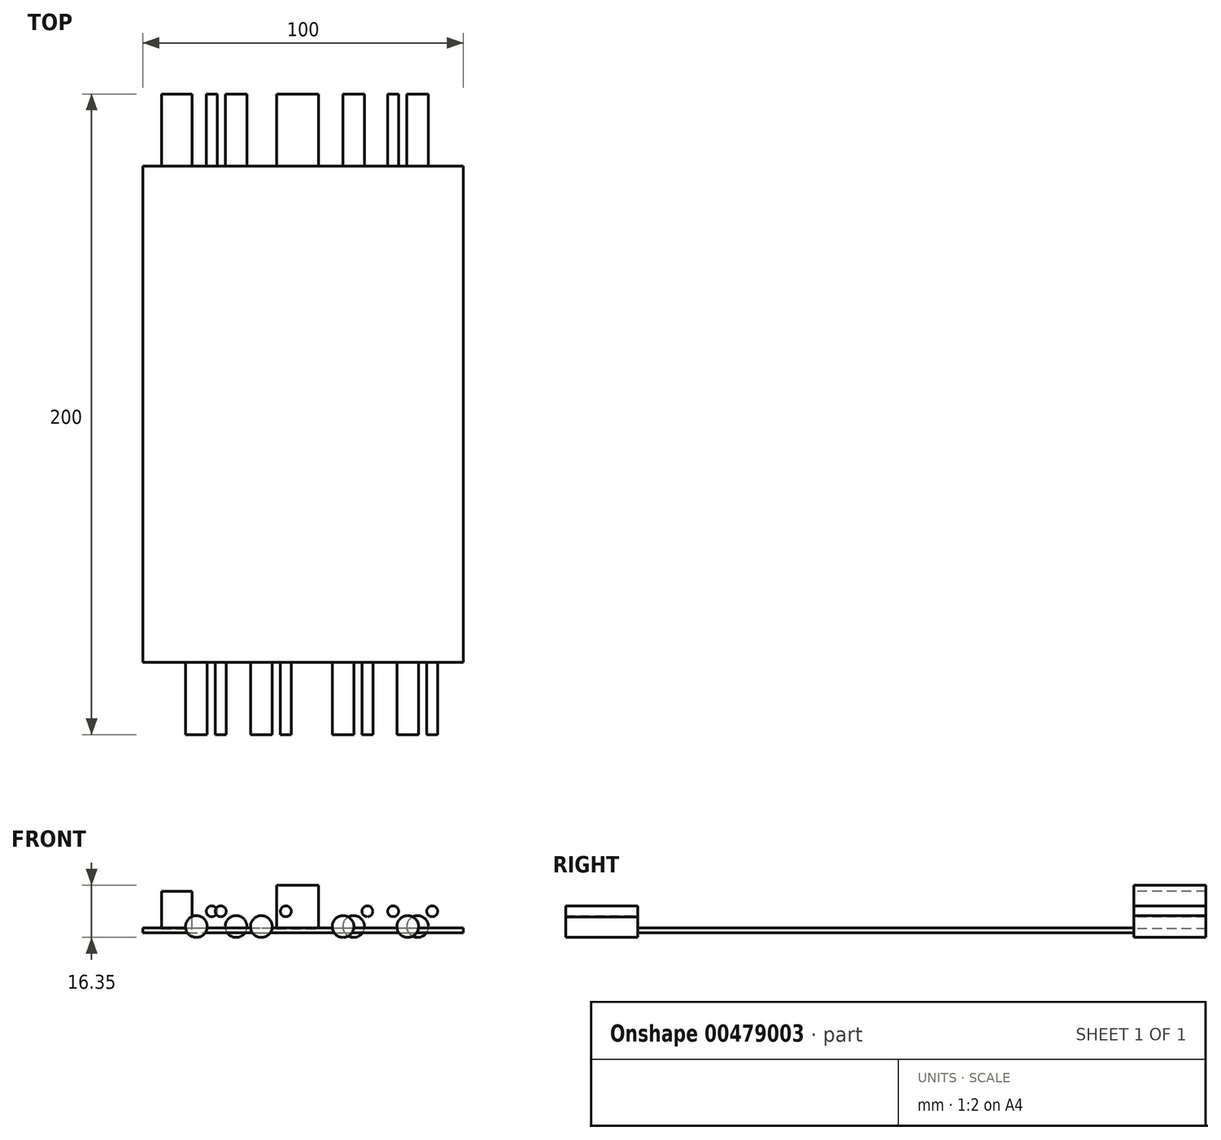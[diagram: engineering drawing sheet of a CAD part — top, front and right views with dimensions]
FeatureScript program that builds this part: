
annotation { "Feature Type Name" : "Feature", "Feature Type Description" : "" }
export const myFeature = defineFeature(function(context is Context, id is Id, definition is map)
    precondition{}
    {
        {
            var Q0;
            Q0=qCreatedBy(makeId("Front.planeOp"),FACE);
            var sketch = newSketch(context, id + "F0", { "sketchPlane" : qUnion([Q0])});
            skCircle(sketch, "E0", {"center": v(-33.3, 2) * mm, "radius": 3.4 * mm});
            skCircle(sketch, "E1", {"center": v(-13, 2) * mm, "radius": 3.4 * mm});
            skCircle(sketch, "E2", {"center": v(12.5, 2) * mm, "radius": 3.4 * mm});
            skCircle(sketch, "E3", {"center": v(32.7, 2) * mm, "radius": 3.4 * mm});
            skCircle(sketch, "E4", {"center": v(-25.7, 6.75) * mm, "radius": 1.7 * mm});
            skCircle(sketch, "E5", {"center": v(-5.35, 6.75) * mm, "radius": 1.7 * mm});
            skCircle(sketch, "E6", {"center": v(20.1, 6.75) * mm, "radius": 1.7 * mm});
            skCircle(sketch, "E7", {"center": v(40.35, 6.75) * mm, "radius": 1.7 * mm});
            skLineSegment(sketch, "E8", {"start": v(50, 43.41) * mm, "end": v(50, -58.7) * mm, "construction": true});
            skLineSegment(sketch, "E9.bottom", {"start": v(50, 1.6) * mm, "end": v(-50, 1.6) * mm, "construction": true});
            skLineSegment(sketch, "E9.top", {"start": v(50, 0) * mm, "end": v(-50, 0) * mm, "construction": true});
            skLineSegment(sketch, "E9.left", {"start": v(50, 1.6) * mm, "end": v(50, 0) * mm, "construction": true});
            skLineSegment(sketch, "E9.right", {"start": v(-50, 1.6) * mm, "end": v(-50, 0) * mm, "construction": true});
            skPoint(sketch, "E9.middle", {"position": v(0, 0.8) * mm});
            skSolve(sketch);
        }
        {
            var Q0;
            Q0=qCreatedBy(makeId("Front.planeOp"),FACE);
            var sketch = newSketch(context, id + "F1", { "sketchPlane" : qUnion([Q0])});
            skCircle(sketch, "E10", {"center": v(35.8, 2) * mm, "radius": 3.4 * mm});
            skCircle(sketch, "E11", {"center": v(15.8, 2) * mm, "radius": 3.4 * mm});
            skCircle(sketch, "E12", {"center": v(-20.9, 2) * mm, "radius": 3.4 * mm});
            skCircle(sketch, "E13", {"center": v(28.15, 6.75) * mm, "radius": 1.7 * mm});
            skCircle(sketch, "E14", {"center": v(-28.5, 6.75) * mm, "radius": 1.7 * mm});
            skLineSegment(sketch, "E15", {"start": v(50, 61.7) * mm, "end": v(50, -52.14) * mm, "construction": true});
            skLineSegment(sketch, "E16.bottom", {"start": v(50, 0) * mm, "end": v(-50, 0) * mm, "construction": true});
            skLineSegment(sketch, "E16.top", {"start": v(50, 1.6) * mm, "end": v(-50, 1.6) * mm, "construction": true});
            skLineSegment(sketch, "E16.left", {"start": v(50, 0) * mm, "end": v(50, 1.6) * mm, "construction": true});
            skLineSegment(sketch, "E16.right", {"start": v(-50, 0) * mm, "end": v(-50, 1.6) * mm, "construction": true});
            skPoint(sketch, "E16.middle", {"position": v(0, 0.8) * mm});
            skLineSegment(sketch, "E17.bottom", {"start": v(-8.25, 1.35) * mm, "end": v(4.85, 1.35) * mm});
            skLineSegment(sketch, "E17.top", {"start": v(-8.25, 14.95) * mm, "end": v(4.85, 14.95) * mm});
            skLineSegment(sketch, "E17.left", {"start": v(-8.25, 1.35) * mm, "end": v(-8.25, 14.95) * mm});
            skLineSegment(sketch, "E17.right", {"start": v(4.85, 1.35) * mm, "end": v(4.85, 14.95) * mm});
            skPoint(sketch, "E17.middle", {"position": v(-1.7, 8.15) * mm});
            skLineSegment(sketch, "E18.bottom", {"start": v(-44.15, 1.35) * mm, "end": v(-34.65, 1.35) * mm});
            skLineSegment(sketch, "E18.top", {"start": v(-44.15, 13.05) * mm, "end": v(-34.65, 13.05) * mm});
            skLineSegment(sketch, "E18.left", {"start": v(-44.15, 1.35) * mm, "end": v(-44.15, 13.05) * mm});
            skLineSegment(sketch, "E18.right", {"start": v(-34.65, 1.35) * mm, "end": v(-34.65, 13.05) * mm});
            skPoint(sketch, "E18.middle", {"position": v(-39.4, 7.2) * mm});
            skSolve(sketch);
        }
        {
            var Q0;
            Q0=qCreatedBy(makeId("Top.planeOp"),FACE);
            var sketch = newSketch(context, id + "F2", { "sketchPlane" : qUnion([Q0])});
            skLineSegment(sketch, "E19.bottom", {"start": v(-50, 77.5) * mm, "end": v(50, 77.5) * mm});
            skLineSegment(sketch, "E19.top", {"start": v(-50, -77.5) * mm, "end": v(50, -77.5) * mm});
            skLineSegment(sketch, "E19.left", {"start": v(-50, 77.5) * mm, "end": v(-50, -77.5) * mm});
            skLineSegment(sketch, "E19.right", {"start": v(50, 77.5) * mm, "end": v(50, -77.5) * mm});
            skPoint(sketch, "E20", {"position": v(50, 0) * mm});
            skSolve(sketch);
        }
        {
            var Q0;
            Q0=makeQuery(id+"F2.imprint","IMPRINT",FACE,{"disambiguationData":[TD([[makeQuery(id+"F2.imprint","IMPRINT",EDGE,{"derivedFrom":sQuery(id+"F2.wireOp",EDGE,"E19.bottom")}),-1.0]])]});
            var Q1;
            Q1=sQuery(id+"F1.wireOp",VERTEX,"E16.left.end");
            extrude(context, id + "F3", {"entities" : qUnion([Q0]), "endBound" : BoundingType.UP_TO_VERTEX, "endBoundEntityVertex" : qUnion([Q1]), "depth" : 0.8 * mm});
        }
        {
            var Q0;
            Q0 = qSketchRegion(id + "F0", true);
            var Q1;
            Q1=makeQuery(id+"F3.opExtrude","SWEPT_FACE",FACE,{"disambiguationData":[OSD([sQuery(id+"F2.wireOp",EDGE,"E19.top")])]});
            extrude(context, id + "F4", {"entities" : qUnion([Q0]), "operationType" : NewBodyOperationType.ADD, "depth" : 100 * mm, "hasSecondDirection" : true, "secondDirectionBound" : SecondDirectionBoundingType.UP_TO_SURFACE, "secondDirectionOppositeDirection" : false, "secondDirectionBoundEntityFace" : qUnion([Q1]), "secondDirectionDepth" : 59.5 * mm});
        }
        {
            var Q0;
            Q0 = qSketchRegion(id + "F1", true);
            var Q1;
            Q1=makeQuery(id+"F3.opExtrude","SWEPT_FACE",FACE,{"disambiguationData":[OSD([sQuery(id+"F2.wireOp",EDGE,"E19.bottom")])]});
            extrude(context, id + "F5", {"entities" : qUnion([Q0]), "operationType" : NewBodyOperationType.ADD, "oppositeDirection" : true, "depth" : 100 * mm, "hasSecondDirection" : true, "secondDirectionBound" : SecondDirectionBoundingType.UP_TO_SURFACE, "secondDirectionOppositeDirection" : true, "secondDirectionBoundEntityFace" : qUnion([Q1]), "secondDirectionDepth" : 25 * mm});
        }
    });
